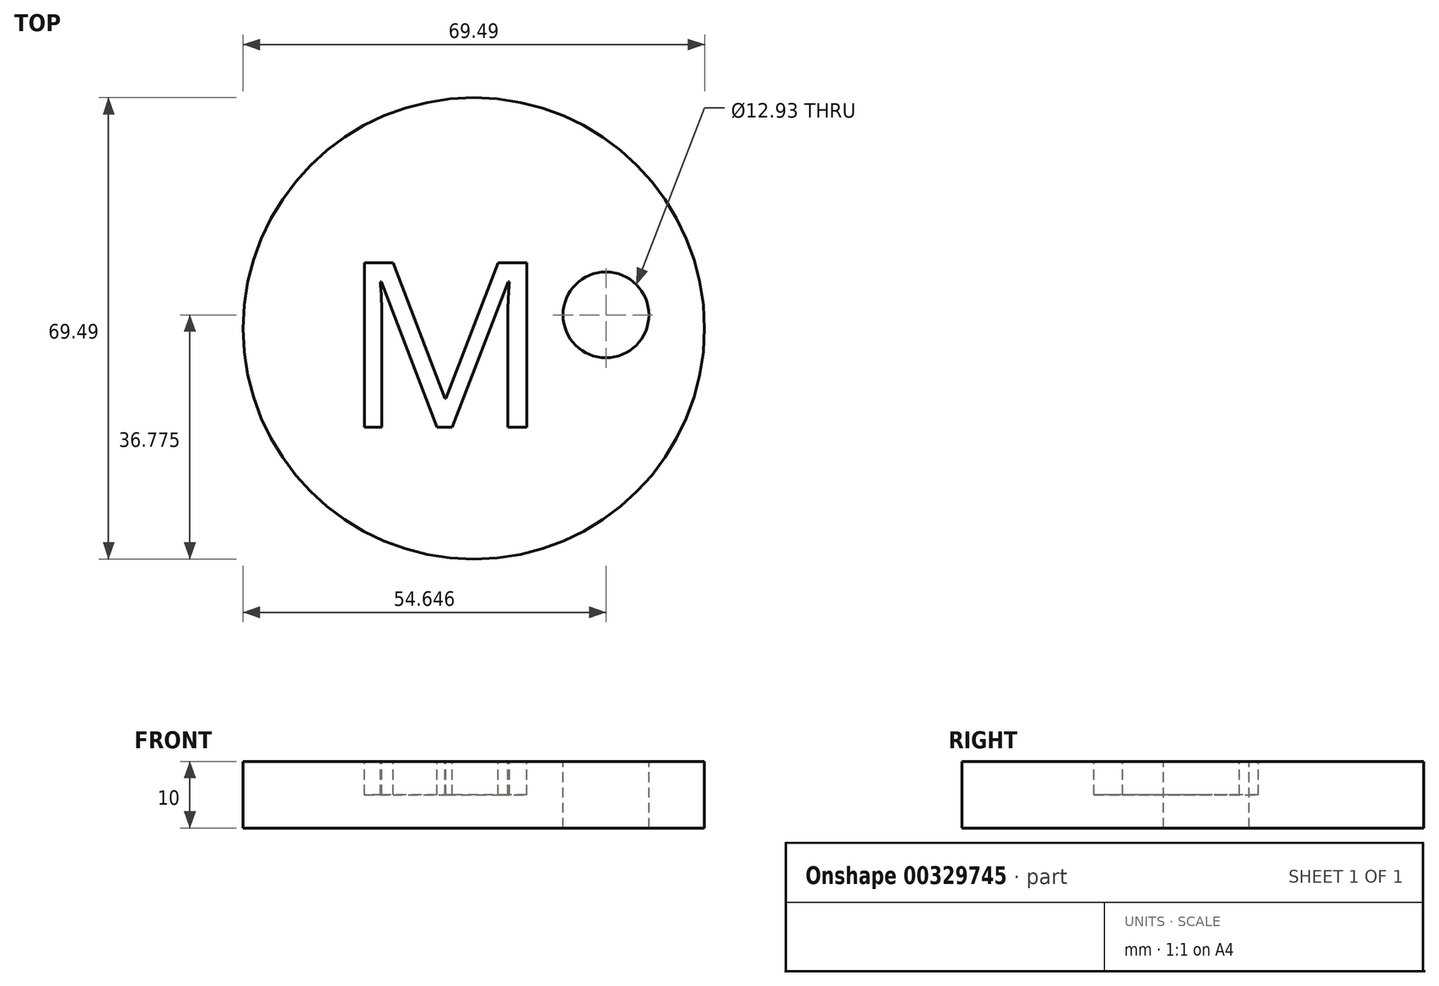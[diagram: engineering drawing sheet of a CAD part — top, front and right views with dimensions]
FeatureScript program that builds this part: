
annotation { "Feature Type Name" : "Feature", "Feature Type Description" : "" }
export const myFeature = defineFeature(function(context is Context, id is Id, definition is map)
    precondition{}
    {
        {
            var Q0;
            Q0=qCreatedBy(makeId("Top.planeOp"),FACE);
            var sketch = newSketch(context, id + "F0", { "sketchPlane" : qUnion([Q0])});
            skCircle(sketch, "E0", {"center": v(-97.1, 34.37) * mm, "radius": 34.74 * mm});
            skSolve(sketch);
        }
        {
            var Q0;
            Q0 = qSketchRegion(id + "F0", true);
            extrude(context, id + "F1", {"entities" : qUnion([Q0]), "depth" : 10 * mm});
        }
        {
            var Q0;
            Q0=makeQuery(id+"F1.opExtrude","CAP_FACE",FACE,{"disambiguationData":[OSD([sQuery(id+"F0.wireOp",EDGE,"E0")])],"isStart":false});
            var sketch = newSketch(context, id + "F2", { "sketchPlane" : qUnion([Q0])});
            skCircle(sketch, "E1", {"center": v(-77.2, 36.4) * mm, "radius": 6.46 * mm});
            skSolve(sketch);
        }
        {
            var Q0;
            Q0 = qSketchRegion(id + "F2", true);
            extrude(context, id + "F3", {"entities" : qUnion([Q0]), "operationType" : NewBodyOperationType.REMOVE, "oppositeDirection" : true, "depth" : 10 * mm});
        }
        {
            var Q0;
            Q0=makeQuery(id+"F1.opExtrude","CAP_FACE",FACE,{"disambiguationData":[OSD([sQuery(id+"F0.wireOp",EDGE,"E0")])],"isStart":false});
            var sketch = newSketch(context, id + "F4", { "sketchPlane" : qUnion([Q0])});
            skText(sketch, "E2", { "text": "M", "fontName": "OpenSans-Regular.ttf"});
            const initialGuessF4  = {"E2": [-0.117, 0.0195, 1, 0, 0.02493]};
            skSetInitialGuess(sketch, initialGuessF4);
            skSolve(sketch);
        }
        {
            var Q0;
            Q0 = qSketchRegion(id + "F4", true);
            extrude(context, id + "F5", {"entities" : qUnion([Q0]), "operationType" : NewBodyOperationType.REMOVE, "oppositeDirection" : true, "depth" : 5 * mm});
        }
    });
